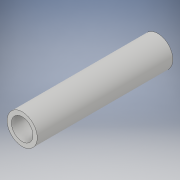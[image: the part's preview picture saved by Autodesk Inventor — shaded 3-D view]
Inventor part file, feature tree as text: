
AUTODESK INVENTOR PART (.ipt)
format: ipt  version: 2019 (Build 230136000, 136)  size: 98,816 bytes
history: native  units: mm
features: extrude x2, sketch x2
ambient origin geometry x8: Origin, YZ Plane, XZ Plane, XY Plane, X Axis, Y Axis, Z Axis, Center Point
bodies: Solid1 (feature_tree)
feature tree (4):
  extrude  "Extrusion1"  Depth=1800.0mm TaperAngle=0.0deg
  extrude  "Extrusion2"  Depth=180.0mm TaperAngle=0.0deg
  sketch  "Sketch1"  dims[d0=400.0mm d1=1800.0mm d2=0.0mm]
  sketch  "Sketch2"  dims[d3=286.0mm d4=180.0mm d5=0.0mm]
